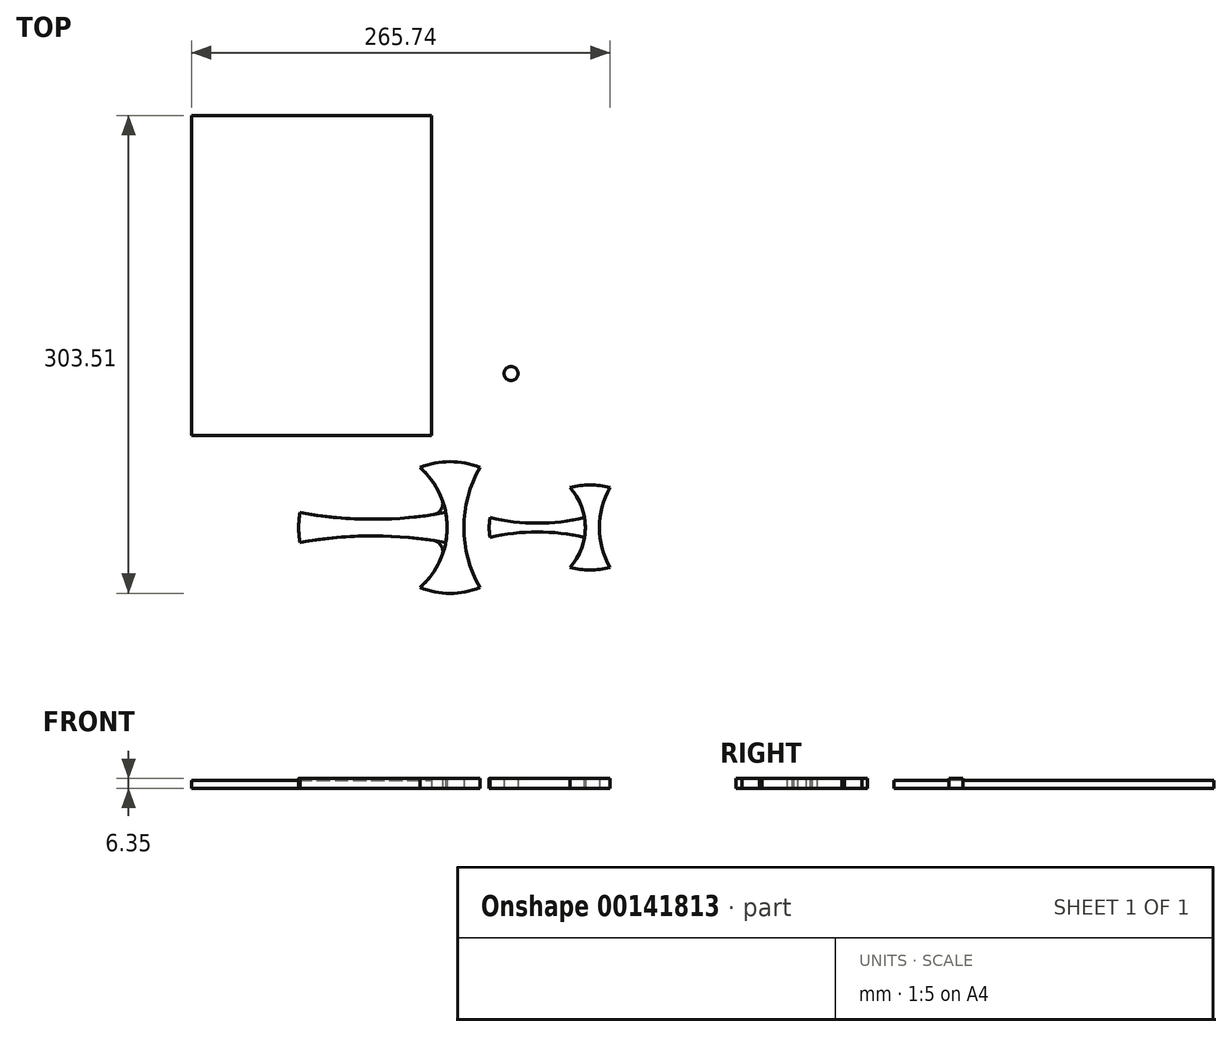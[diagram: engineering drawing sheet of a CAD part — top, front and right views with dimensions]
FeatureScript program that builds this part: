
annotation { "Feature Type Name" : "Feature", "Feature Type Description" : "" }
export const myFeature = defineFeature(function(context is Context, id is Id, definition is map)
    precondition{}
    {
        {
            var Q0;
            Q0=qCreatedBy(makeId("Top.planeOp"),FACE);
            var sketch = newSketch(context, id + "F0", { "sketchPlane" : qUnion([Q0])});
            skLineSegment(sketch, "E0.bottom", {"start": v(-44.45, 38.1) * mm, "end": v(-6.35, 38.1) * mm, "construction": true});
            skLineSegment(sketch, "E0.top", {"start": v(-44.45, -38.1) * mm, "end": v(-6.35, -38.1) * mm, "construction": true});
            skLineSegment(sketch, "E0.left", {"start": v(-44.45, 38.1) * mm, "end": v(-44.45, -38.1) * mm, "construction": true});
            skLineSegment(sketch, "E0.right", {"start": v(-6.35, 38.1) * mm, "end": v(-6.35, -38.1) * mm, "construction": true});
            skLineSegment(sketch, "E1", {"start": v(-6.35, 0) * mm, "end": v(-120.65, 0) * mm, "construction": true});
            skLineSegment(sketch, "E2", {"start": v(-120.65, 9.53) * mm, "end": v(-120.65, -9.53) * mm, "construction": true});
            skArc(sketch, "E3", {"start": v(-6.35, 38.1) * mm, "mid": v(-25.4, 41.8) * mm, "end": v(-44.45, 38.1) * mm});
            skArc(sketch, "E4", {"start": v(-44.45, -38.1) * mm, "mid": v(-25.4, -41.8) * mm, "end": v(-6.35, -38.1) * mm});
            skArc(sketch, "E5", {"start": v(-6.35, 38.1) * mm, "mid": v(-16.56, 0) * mm, "end": v(-6.35, -38.1) * mm});
            skArc(sketch, "E6", {"start": v(-44.45, -38.1) * mm, "mid": v(-27.25, 0) * mm, "end": v(-44.45, 38.1) * mm});
            skArc(sketch, "E7", {"start": v(-120.65, 9.53) * mm, "mid": v(-74.4, 5.28) * mm, "end": v(-28.15, 9.53) * mm});
            skArc(sketch, "E8", {"start": v(-28.15, -9.53) * mm, "mid": v(-74.4, -5.28) * mm, "end": v(-120.65, -9.53) * mm});
            skArc(sketch, "E9", {"start": v(-120.65, 9.53) * mm, "mid": v(-121.55, 0) * mm, "end": v(-120.65, -9.53) * mm});
            skSolve(sketch);
        }
        {
            var Q0;
            {var subQ0=sQuery(id+"F0.wireOp",EDGE,"E7");Q0=makeQuery(id+"F0.imprint","IMPRINT",FACE,{"disambiguationData":[TD([[makeQuery(id+"F0.imprint","IMPRINT",EDGE,{"derivedFrom":subQ0}),-1.0]])]});}
            var Q1;
            {var subQ3=sQuery(id+"F0.wireOp",EDGE,"E3");Q1=makeQuery(id+"F0.imprint","IMPRINT",FACE,{"disambiguationData":[TD([[makeQuery(id+"F0.imprint","IMPRINT",EDGE,{"derivedFrom":subQ3}),1.0]])]});}
            extrude(context, id + "F1", {"entities" : qUnion([Q0, Q1]), "depth" : 6.35 * mm});
        }
        {
            var Q0;
            Q0=makeQuery(id+"F1.opExtrude","SWEPT_EDGE",EDGE,{"disambiguationData":[OSD([sQuery(id+"F0.wireOp",EDGE,"E6"),sQuery(id+"F0.wireOp",EDGE,"E7")])]});
            var Q1;
            Q1=makeQuery(id+"F1.opExtrude","SWEPT_EDGE",EDGE,{"disambiguationData":[OSD([sQuery(id+"F0.wireOp",EDGE,"E6"),sQuery(id+"F0.wireOp",EDGE,"E8")])]});
            fillet(context, id + "F2", {"entities" : qUnion([Q0, Q1]), "radius" : 7.11 * mm, "tangentPropagation" : true, "allowEdgeOverflow" : false});
        }
        {
            var Q0;
            Q0=qCreatedBy(makeId("Top.planeOp"),FACE);
            var sketch = newSketch(context, id + "F3", { "sketchPlane" : qUnion([Q0])});
            skLineSegment(sketch, "E10.bottom", {"start": v(50.8, 25.4) * mm, "end": v(76.2, 25.4) * mm, "construction": true});
            skLineSegment(sketch, "E10.top", {"start": v(50.8, -25.4) * mm, "end": v(76.2, -25.4) * mm, "construction": true});
            skLineSegment(sketch, "E10.left", {"start": v(50.8, 25.4) * mm, "end": v(50.8, -25.4) * mm, "construction": true});
            skLineSegment(sketch, "E10.right", {"start": v(76.2, 25.4) * mm, "end": v(76.2, -25.4) * mm, "construction": true});
            skLineSegment(sketch, "E11", {"start": v(76.2, 0) * mm, "end": v(0, 0) * mm, "construction": true});
            skLineSegment(sketch, "E12", {"start": v(0, 6.35) * mm, "end": v(0, -6.35) * mm, "construction": true});
            skArc(sketch, "E13", {"start": v(76.2, 25.4) * mm, "mid": v(63.5, 27.01) * mm, "end": v(50.8, 25.4) * mm});
            skArc(sketch, "E14", {"start": v(50.8, -25.4) * mm, "mid": v(63.5, -27.01) * mm, "end": v(76.2, -25.4) * mm});
            skArc(sketch, "E15", {"start": v(76.2, 25.4) * mm, "mid": v(69.4, 0) * mm, "end": v(76.2, -25.4) * mm});
            skArc(sketch, "E16", {"start": v(50.8, -25.4) * mm, "mid": v(60.5, 0) * mm, "end": v(50.8, 25.4) * mm});
            skArc(sketch, "E17", {"start": v(0, 6.35) * mm, "mid": v(29.98, 2.76) * mm, "end": v(59.97, 6.35) * mm});
            skArc(sketch, "E18", {"start": v(59.97, -6.35) * mm, "mid": v(29.98, -2.76) * mm, "end": v(0, -6.35) * mm});
            skArc(sketch, "E19", {"start": v(0, 6.35) * mm, "mid": v(-0.53, 0) * mm, "end": v(0, -6.35) * mm});
            skSolve(sketch);
        }
        {
            var Q0;
            {var subQ0=sQuery(id+"F3.wireOp",EDGE,"E17");Q0=makeQuery(id+"F3.imprint","IMPRINT",FACE,{"disambiguationData":[TD([[makeQuery(id+"F3.imprint","IMPRINT",EDGE,{"derivedFrom":subQ0}),-1.0]])]});}
            var Q1;
            {var subQ3=sQuery(id+"F3.wireOp",EDGE,"E13");Q1=makeQuery(id+"F3.imprint","IMPRINT",FACE,{"disambiguationData":[TD([[makeQuery(id+"F3.imprint","IMPRINT",EDGE,{"derivedFrom":subQ3}),1.0]])]});}
            extrude(context, id + "F4", {"entities" : qUnion([Q0, Q1]), "depth" : 6.35 * mm});
        }
        {
            var Q0;
            Q0=makeQuery(id+"F4.opExtrude","SWEPT_EDGE",EDGE,{"disambiguationData":[OSD([sQuery(id+"F3.wireOp",EDGE,"E16"),sQuery(id+"F3.wireOp",EDGE,"E18")])]});
            var Q1;
            Q1=makeQuery(id+"F4.opExtrude","SWEPT_EDGE",EDGE,{"disambiguationData":[OSD([sQuery(id+"F3.wireOp",EDGE,"E16"),sQuery(id+"F3.wireOp",EDGE,"E17")])]});
            fillet(context, id + "F5", {"entities" : qUnion([Q0, Q1]), "radius" : .57 / 50.8 * mm, "tangentPropagation" : true, "allowEdgeOverflow" : false});
        }
        {
            var Q0;
            {var subQ3=sQuery(id+"F0.wireOp",EDGE,"E3");Q0=makeQuery(id+"F0.imprint","IMPRINT",FACE,{"disambiguationData":[TD([[makeQuery(id+"F0.imprint","IMPRINT",EDGE,{"derivedFrom":subQ3}),1.0]])]});}
            extrude(context, id + "F6", {"entities" : qUnion([Q0]), "depth" : 6.35 * mm});
        }
        {
            var Q0;
            {var subQ0=sQuery(id+"F0.wireOp",EDGE,"E7");Q0=makeQuery(id+"F0.imprint","IMPRINT",FACE,{"disambiguationData":[TD([[makeQuery(id+"F0.imprint","IMPRINT",EDGE,{"derivedFrom":subQ0}),-1.0]])]});}
            extrude(context, id + "F7", {"entities" : qUnion([Q0]), "depth" : 6.35 * mm});
        }
        {
            var Q0;
            {var subQ3=sQuery(id+"F3.wireOp",EDGE,"E13");Q0=makeQuery(id+"F3.imprint","IMPRINT",FACE,{"disambiguationData":[TD([[makeQuery(id+"F3.imprint","IMPRINT",EDGE,{"derivedFrom":subQ3}),1.0]])]});}
            extrude(context, id + "F8", {"entities" : qUnion([Q0]), "depth" : 6.35 * mm});
        }
        {
            var Q0;
            {var subQ0=sQuery(id+"F3.wireOp",EDGE,"E17");Q0=makeQuery(id+"F3.imprint","IMPRINT",FACE,{"disambiguationData":[TD([[makeQuery(id+"F3.imprint","IMPRINT",EDGE,{"derivedFrom":subQ0}),-1.0]])]});}
            extrude(context, id + "F9", {"entities" : qUnion([Q0]), "depth" : 6.35 * mm});
        }
        {
            var Q0;
            Q0=qCreatedBy(makeId("Top.planeOp"),FACE);
            var sketch = newSketch(context, id + "F10", { "sketchPlane" : qUnion([Q0])});
            skLineSegment(sketch, "E20.bottom", {"start": v(-189.54, 261.7) * mm, "end": v(-37.14, 261.7) * mm});
            skLineSegment(sketch, "E20.top", {"start": v(-189.54, 58.5) * mm, "end": v(-37.14, 58.5) * mm});
            skLineSegment(sketch, "E20.left", {"start": v(-189.54, 261.7) * mm, "end": v(-189.54, 58.5) * mm});
            skLineSegment(sketch, "E20.right", {"start": v(-37.14, 261.7) * mm, "end": v(-37.14, 58.5) * mm});
            skSolve(sketch);
        }
        {
            var Q0;
            Q0=makeQuery(id+"F10.imprint","IMPRINT",FACE,{"disambiguationData":[TD([[makeQuery(id+"F10.imprint","IMPRINT",EDGE,{"derivedFrom":sQuery(id+"F10.wireOp",EDGE,"E20.bottom")}),-1.0]])]});
            extrude(context, id + "F11", {"entities" : qUnion([Q0]), "depth" : 5.08 * mm});
        }
        {
            var Q0;
            Q0=qCreatedBy(makeId("Top.planeOp"),FACE);
            var sketch = newSketch(context, id + "F12", { "sketchPlane" : qUnion([Q0])});
            skCircle(sketch, "E21", {"center": v(13.39, 97.82) * mm, "radius": 4.45 * mm});
            skSolve(sketch);
        }
        {
            var Q0;
            Q0=makeQuery(id+"F12.imprint","IMPRINT",FACE,{"disambiguationData":[TD([[makeQuery(id+"F12.imprint","IMPRINT",EDGE,{"derivedFrom":sQuery(id+"F12.wireOp",EDGE,"E21")}),1.0]])]});
            extrude(context, id + "F13", {"entities" : qUnion([Q0]), "depth" : 6.35 * mm});
        }
    });
